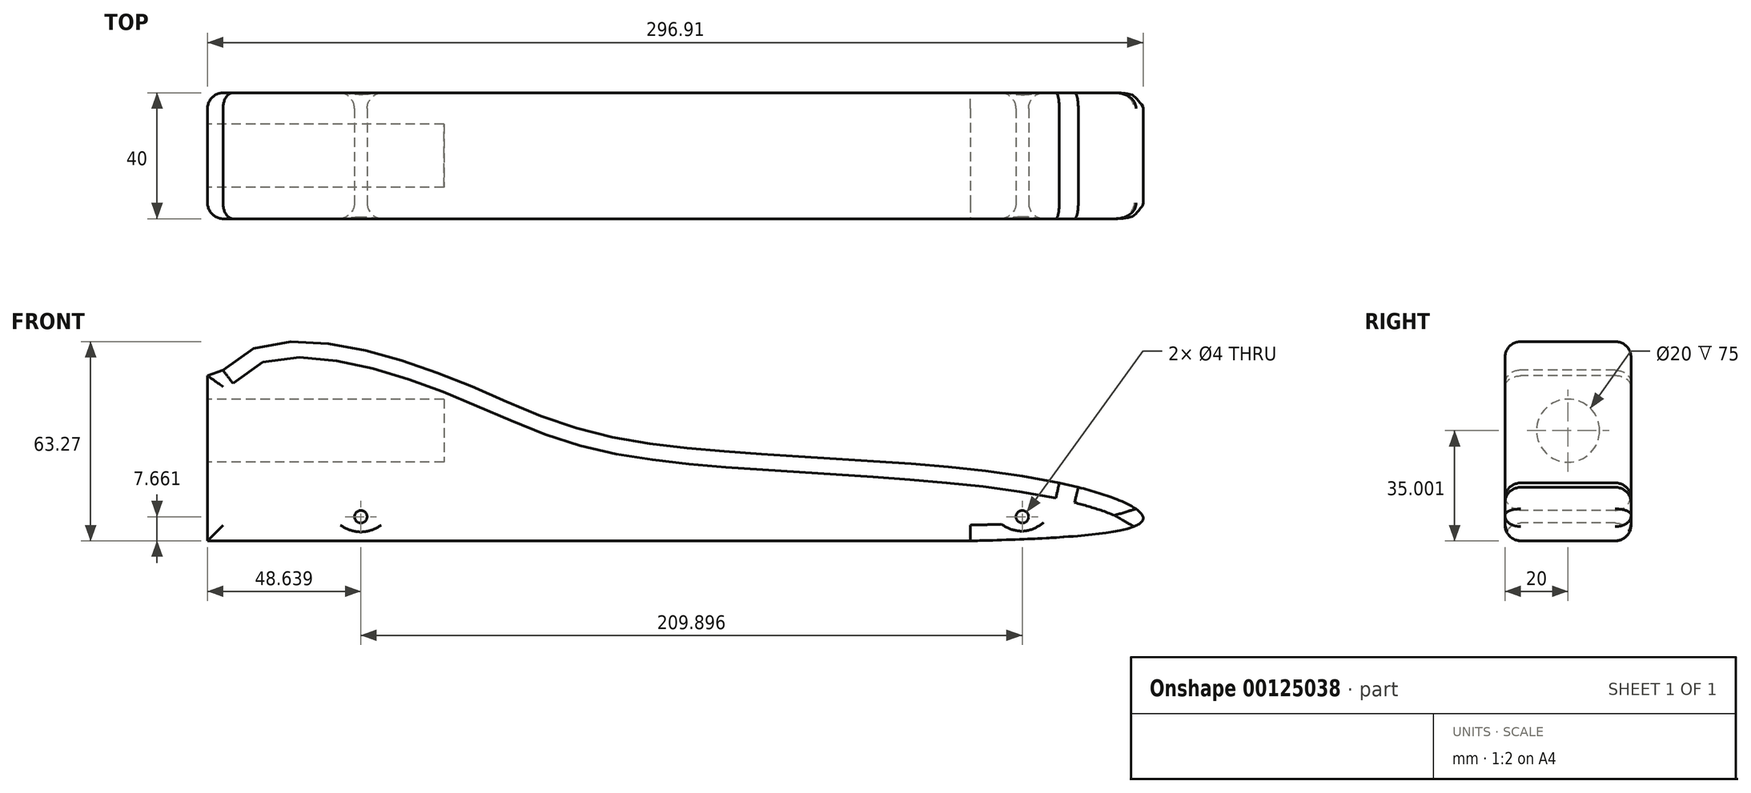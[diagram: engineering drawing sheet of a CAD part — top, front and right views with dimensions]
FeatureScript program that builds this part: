
annotation { "Feature Type Name" : "Feature", "Feature Type Description" : "" }
export const myFeature = defineFeature(function(context is Context, id is Id, definition is map)
    precondition{}
    {
        {
            var Q0;
            Q0=qCreatedBy(makeId("Front.planeOp"),FACE);
            var sketch = newSketch(context, id + "F0", { "sketchPlane" : qUnion([Q0])});
            skLineSegment(sketch, "E0.bottom", {"start": v(-84.2, -32.3) * mm, "end": v(215.8, -32.3) * mm});
            skLineSegment(sketch, "E0.top", {"start": v(-84.2, 37.7) * mm, "end": v(215.8, 37.7) * mm});
            skLineSegment(sketch, "E0.left", {"start": v(-84.2, -32.3) * mm, "end": v(-84.2, 37.7) * mm});
            skLineSegment(sketch, "E0.right", {"start": v(215.8, -32.3) * mm, "end": v(215.8, 37.7) * mm});
            skSolve(sketch);
        }
        {
            var Q0;
            Q0=makeQuery(id+"F0.imprint","IMPRINT",FACE,{"disambiguationData":[TD([[makeQuery(id+"F0.imprint","IMPRINT",EDGE,{"derivedFrom":sQuery(id+"F0.wireOp",EDGE,"E0.bottom")}),1.0]])]});
            extrude(context, id + "F1", {"entities" : qUnion([Q0]), "depth" : 40 * mm});
        }
        {
            var Q0;
            Q0=makeQuery(id+"F1.opExtrude","SWEPT_FACE",FACE,{"disambiguationData":[OSD([sQuery(id+"F0.wireOp",EDGE,"E0.left")])]});
            var sketch = newSketch(context, id + "F2", { "sketchPlane" : qUnion([Q0])});
            skCircle(sketch, "E1", {"center": v(20, 2.7) * mm, "radius": 10 * mm});
            skSolve(sketch);
        }
        {
            var Q0;
            Q0=makeQuery(id+"F2.imprint","IMPRINT",FACE,{"disambiguationData":[TD([[makeQuery(id+"F2.imprint","IMPRINT",EDGE,{"derivedFrom":sQuery(id+"F2.wireOp",EDGE,"E1")}),1.0]])]});
            extrude(context, id + "F3", {"entities" : qUnion([Q0]), "operationType" : NewBodyOperationType.REMOVE, "oppositeDirection" : true, "depth" : 75 * mm});
        }
        {
            var Q0;
            Q0=makeQuery(id+"F1.opExtrude","CAP_FACE",FACE,{"disambiguationData":[OSD([sQuery(id+"F0.wireOp",EDGE,"E0.bottom"),sQuery(id+"F0.wireOp",EDGE,"E0.top"),sQuery(id+"F0.wireOp",EDGE,"E0.left"),sQuery(id+"F0.wireOp",EDGE,"E0.right")])],"isStart":false});
            var sketch = newSketch(context, id + "F4", { "sketchPlane" : qUnion([Q0])});
            skCircle(sketch, "E2", {"center": v(-35.56, -24.64) * mm, "radius": 2 * mm});
            skCircle(sketch, "E3", {"center": v(174.33, -24.64) * mm, "radius": 2 * mm});
            skLineSegment(sketch, "E4", {"start": v(-35.56, 37.7) * mm, "end": v(-84.2, 20.1) * mm});
            skLineSegment(sketch, "E5", {"start": v(-35.56, 37.7) * mm, "end": v(215.8, -20.83) * mm});
            skSolve(sketch);
        }
        {
            var Q0;
            Q0=makeQuery(id+"F4.imprint","IMPRINT",FACE,{"disambiguationData":[TD([[makeQuery(id+"F4.imprint","IMPRINT",EDGE,{"derivedFrom":sQuery(id+"F4.wireOp",EDGE,"E2")}),1.0]])]});
            var Q1;
            Q1=makeQuery(id+"F4.imprint","IMPRINT",FACE,{"disambiguationData":[TD([[makeQuery(id+"F4.imprint","IMPRINT",EDGE,{"derivedFrom":sQuery(id+"F4.wireOp",EDGE,"E3")}),1.0]])]});
            extrude(context, id + "F5", {"entities" : qUnion([Q0, Q1]), "operationType" : NewBodyOperationType.REMOVE, "endBound" : BoundingType.THROUGH_ALL, "oppositeDirection" : true, "depth" : 25 * mm});
        }
        {
            var Q0;
            {var subQ1=sQuery(id+"F4.wireOp",EDGE,"E5");Q0=makeQuery(id+"F4.imprint","IMPRINT",FACE,{"disambiguationData":[TD([[makeQuery(id+"F4.imprint","IMPRINT",EDGE,{"derivedFrom":subQ1}),1.0]])]});}
            extrude(context, id + "F6", {"entities" : qUnion([Q0]), "operationType" : NewBodyOperationType.REMOVE, "endBound" : BoundingType.THROUGH_ALL, "oppositeDirection" : true, "depth" : 25 * mm});
        }
        {
            var Q0;
            Q0=makeQuery(id+"F1.opExtrude","SWEPT_FACE",FACE,{"disambiguationData":[OSD([sQuery(id+"F0.wireOp",EDGE,"E0.top")])]});
            var sketch = newSketch(context, id + "F7", { "sketchPlane" : qUnion([Q0])});
            skLineSegment(sketch, "E6", {"start": v(-35.56, -10) * mm, "end": v(-84.2, -10) * mm});
            skLineSegment(sketch, "E7", {"start": v(-84.2, -30) * mm, "end": v(-35.56, -30) * mm});
            skSolve(sketch);
        }
        {
            var Q0;
            Q0=makeQuery(id+"F4.imprint","IMPRINT",FACE,{"disambiguationData":[TD([[makeQuery(id+"F4.imprint","IMPRINT",EDGE,{"derivedFrom":sQuery(id+"F4.wireOp",EDGE,"E2")}),-1.0]])]});
            var sketch = newSketch(context, id + "F8", { "sketchPlane" : qUnion([Q0])});
            skPoint(sketch, "E8.0", {"position": v(210.8, -27.3) * mm});
            skPoint(sketch, "E9.0", {"position": v(-79.2, 32.7) * mm});
            skLineSegment(sketch, "E10.0", {"start": v(-35.56, 37.7) * mm, "end": v(215.8, -20.83) * mm});
            skLineSegment(sketch, "E11.0", {"start": v(-84.2, 37.7) * mm, "end": v(-35.56, 37.7) * mm});
            skLineSegment(sketch, "E12.0", {"start": v(-84.2, -32.3) * mm, "end": v(-84.2, 37.7) * mm});
            skLineSegment(sketch, "E13.0", {"start": v(215.8, -32.3) * mm, "end": v(-84.2, -32.3) * mm});
            skLineSegment(sketch, "E14.0", {"start": v(215.8, -20.83) * mm, "end": v(215.8, -32.3) * mm});
            skLineSegment(sketch, "E15", {"start": v(-84.2, 12.7) * mm, "end": v(-9.2, 12.7) * mm});
            skLineSegment(sketch, "E16", {"start": v(-9.2, -7.3) * mm, "end": v(-84.2, -7.3) * mm});
            skFitSpline(sketch, "E17", {"points": [v(-79.2, 21.97) * mm, v(-9.2, 20.26) * mm, v(47.26, 0) * mm, v(186.07, -13.9) * mm, v(210.8, -27.3) * mm, v(-79.2, -32.3) * mm, v(-84.2, -32.3) * mm, v(-79.2, 21.97) * mm]});
            skSolve(sketch);
        }
        {
            var Q0;
            {var subQ0=sQuery(id+"F8.wireOp",EDGE,"E10.0");var subQ3=sQuery(id+"F8.wireOp",EDGE,"E17");var subQ4=makeQuery(id+"F8.imprint","INTERSECT",VERTEX,{"disambiguationData":[OD(0.0)],"derivedFrom":[subQ0,subQ3]});Q0=makeQuery(id+"F8.imprint","IMPRINT",FACE,{"disambiguationData":[TD([[makeQuery(id+"F8.imprint","IMPRINT",EDGE,{"disambiguationData":[TD([[subQ4,1.0]])],"derivedFrom":subQ3}),1.0]])]});}
            var Q1;
            {var subQ0=sQuery(id+"F8.wireOp",EDGE,"E11.0");Q1=makeQuery(id+"F8.imprint","IMPRINT",FACE,{"disambiguationData":[TD([[makeQuery(id+"F8.imprint","IMPRINT",EDGE,{"derivedFrom":subQ0}),-1.0]])]});}
            var Q2;
            {var subQ0=sQuery(id+"F8.wireOp",EDGE,"E14.0");Q2=makeQuery(id+"F8.imprint","IMPRINT",FACE,{"disambiguationData":[TD([[makeQuery(id+"F8.imprint","IMPRINT",EDGE,{"derivedFrom":subQ0}),1.0]])]});}
            extrude(context, id + "F9", {"entities" : qUnion([Q0, Q1, Q2]), "operationType" : NewBodyOperationType.REMOVE, "endBound" : BoundingType.THROUGH_ALL, "oppositeDirection" : true, "depth" : 25.4 * mm});
        }
        {
            var Q0;
            Q0=makeQuery(id+"F1.opExtrude","CAP_FACE",FACE,{"disambiguationData":[OSD([sQuery(id+"F0.wireOp",EDGE,"E0.bottom"),sQuery(id+"F0.wireOp",EDGE,"E0.top"),sQuery(id+"F0.wireOp",EDGE,"E0.left"),sQuery(id+"F0.wireOp",EDGE,"E0.right")])],"isStart":false});
            var Q1;
            Q1=makeQuery(id+"F1.opExtrude","CAP_FACE",FACE,{"disambiguationData":[OSD([sQuery(id+"F0.wireOp",EDGE,"E0.bottom"),sQuery(id+"F0.wireOp",EDGE,"E0.top"),sQuery(id+"F0.wireOp",EDGE,"E0.left"),sQuery(id+"F0.wireOp",EDGE,"E0.right")])],"isStart":true});
            fillet(context, id + "F10", {"entities" : qUnion([Q0, Q1]), "radius" : 5 * mm, "tangentPropagation" : true, "allowEdgeOverflow" : false});
        }
    });
